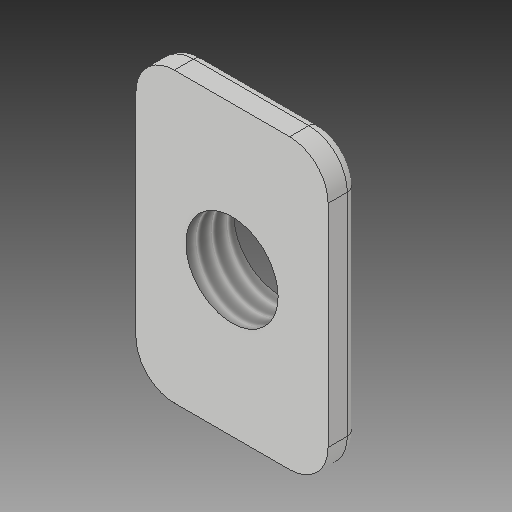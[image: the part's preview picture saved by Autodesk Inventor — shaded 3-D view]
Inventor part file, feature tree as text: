
AUTODESK INVENTOR PART (.ipt)
format: ipt  version: 2017 (Build 210142000, 142)  size: 144,384 bytes
history: native  units: mm
features: other x3, sketch x2
ambient origin geometry x8: Origin, YZ Plane, XZ Plane, XY Plane, X Axis, Y Axis, Z Axis, Center Point
bodies: Solid1 (feature_tree)
feature tree (5):
  other  "M5 Tee Nut_MIR_MIR.ipt"
  other  "Solid1::M5 Tee Nut_MIR_MIR.ipt"
  other  "TaggingFeature1"
  sketch  "Sketch1"  dims[d0=10.0mm]
  sketch  "Sketch2"
